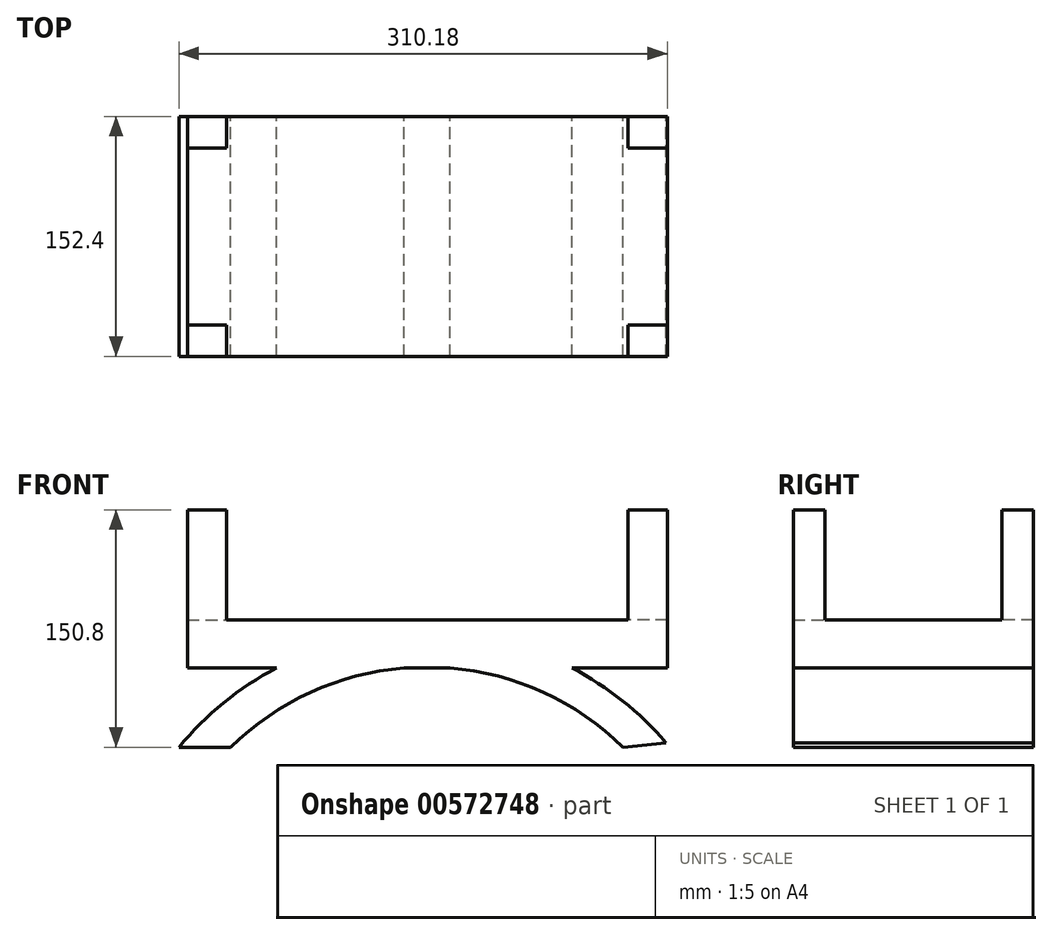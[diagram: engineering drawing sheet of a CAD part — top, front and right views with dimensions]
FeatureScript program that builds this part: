
annotation { "Feature Type Name" : "Feature", "Feature Type Description" : "" }
export const myFeature = defineFeature(function(context is Context, id is Id, definition is map)
    precondition{}
    {
        {
            var Q0;
            Q0=qCreatedBy(makeId("Front.planeOp"),FACE);
            var sketch = newSketch(context, id + "F0", { "sketchPlane" : qUnion([Q0])});
            skLineSegment(sketch, "E0.bottom", {"start": v(152.4, 15.24) * mm, "end": v(-152.4, 15.24) * mm});
            skLineSegment(sketch, "E0.top", {"start": v(152.4, -15.24) * mm, "end": v(-152.4, -15.24) * mm});
            skLineSegment(sketch, "E0.left", {"start": v(152.4, 15.24) * mm, "end": v(152.4, -15.24) * mm});
            skLineSegment(sketch, "E0.right", {"start": v(-152.4, 15.24) * mm, "end": v(-152.4, -15.24) * mm});
            skPoint(sketch, "E0.middle", {"position": v(0, 0) * mm});
            skSolve(sketch);
        }
        {
            var Q0;
            Q0=makeQuery(id+"F0.imprint","IMPRINT",FACE,{"disambiguationData":[TD([[makeQuery(id+"F0.imprint","IMPRINT",EDGE,{"derivedFrom":sQuery(id+"F0.wireOp",EDGE,"E0.bottom")}),1.0]])]});
            extrude(context, id + "F1", {"entities" : qUnion([Q0]), "depth" : 152.4 * mm, "offsetDistance" : 25.4 * mm});
        }
        {
            var Q0;
            Q0=makeQuery(id+"F1.opExtrude","SWEPT_FACE",FACE,{"disambiguationData":[OSD([sQuery(id+"F0.wireOp",EDGE,"E0.bottom")])]});
            var sketch = newSketch(context, id + "F2", { "sketchPlane" : qUnion([Q0])});
            skLineSegment(sketch, "E1.bottom", {"start": v(-152.4, 0) * mm, "end": v(-127.4, 0) * mm});
            skLineSegment(sketch, "E1.top", {"start": v(-152.4, -20) * mm, "end": v(-127.4, -20) * mm});
            skLineSegment(sketch, "E1.left", {"start": v(-152.4, 0) * mm, "end": v(-152.4, -20) * mm});
            skLineSegment(sketch, "E1.right", {"start": v(-127.4, 0) * mm, "end": v(-127.4, -20) * mm});
            skLineSegment(sketch, "E2.bottom", {"start": v(-152.4, -152.4) * mm, "end": v(-127.4, -152.4) * mm});
            skLineSegment(sketch, "E2.top", {"start": v(-152.4, -132.4) * mm, "end": v(-127.4, -132.4) * mm});
            skLineSegment(sketch, "E2.left", {"start": v(-152.4, -152.4) * mm, "end": v(-152.4, -132.4) * mm});
            skLineSegment(sketch, "E2.right", {"start": v(-127.4, -152.4) * mm, "end": v(-127.4, -132.4) * mm});
            skLineSegment(sketch, "E3.bottom", {"start": v(152.4, 0) * mm, "end": v(127.4, 0) * mm});
            skLineSegment(sketch, "E3.top", {"start": v(152.4, -20) * mm, "end": v(127.4, -20) * mm});
            skLineSegment(sketch, "E3.left", {"start": v(152.4, 0) * mm, "end": v(152.4, -20) * mm});
            skLineSegment(sketch, "E3.right", {"start": v(127.4, 0) * mm, "end": v(127.4, -20) * mm});
            skLineSegment(sketch, "E4.bottom", {"start": v(152.4, -152.4) * mm, "end": v(127.4, -152.4) * mm});
            skLineSegment(sketch, "E4.top", {"start": v(152.4, -132.4) * mm, "end": v(127.4, -132.4) * mm});
            skLineSegment(sketch, "E4.left", {"start": v(152.4, -152.4) * mm, "end": v(152.4, -132.4) * mm});
            skLineSegment(sketch, "E4.right", {"start": v(127.4, -152.4) * mm, "end": v(127.4, -132.4) * mm});
            skSolve(sketch);
        }
        {
            var Q0;
            Q0=qSketchRegion(id+"F2",true);
            extrude(context, id + "F3", {"entities" : qUnion([Q0]), "operationType" : NewBodyOperationType.ADD, "depth" : 70 * mm, "offsetDistance" : 25 * mm});
        }
        {
            var Q0;
            Q0=qCreatedBy(makeId("Front.planeOp"),FACE);
            var sketch = newSketch(context, id + "F4", { "sketchPlane" : qUnion([Q0])});
            skArc(sketch, "E5", {"start": v(151.54, -62.73) * mm, "mid": v(-3.78, 7.87) * mm, "end": v(-157.78, -65.56) * mm});
            skLineSegment(sketch, "E6", {"start": v(-157.78, -65.56) * mm, "end": v(-124.87, -65.56) * mm});
            skLineSegment(sketch, "E7", {"start": v(124.23, -65.56) * mm, "end": v(151.54, -62.73) * mm});
            skArc(sketch, "E8", {"start": v(124.23, -65.56) * mm, "mid": v(-0.32, -14.65) * mm, "end": v(-124.87, -65.56) * mm});
            skSolve(sketch);
        }
        {
            var Q0;
            Q0=makeQuery(id+"F4.imprint","IMPRINT",FACE,{"disambiguationData":[TD([[makeQuery(id+"F4.imprint","IMPRINT",EDGE,{"derivedFrom":sQuery(id+"F4.wireOp",EDGE,"E5")}),1.0]])]});
            extrude(context, id + "F5", {"entities" : qUnion([Q0]), "operationType" : NewBodyOperationType.ADD, "depth" : 152.4 * mm, "offsetDistance" : 25.4 * mm});
        }
        {
            var Q0;
            Q0=qCreatedBy(makeId("Front.planeOp"),FACE);
            var sketch = newSketch(context, id + "F6", { "sketchPlane" : qUnion([Q0])});
            skLineSegment(sketch, "E9", {"start": v(-148.6, -3.82) * mm, "end": v(-148.6, -55.17) * mm});
            skSolve(sketch);
        }
        {
            var Q0;
            Q0=qSketchRegion(id+"F6",true);
            var Q1;
            Q1=sQuery(id+"F6.wireOp",EDGE,"E9");
            extrude(context, id + "F7", {"entities" : qUnion([Q0]), "bodyType" : ToolBodyType.SURFACE, "operationType" : NewBodyOperationType.ADD, "surfaceEntities" : qUnion([Q1]), "depth" : 152.4 * mm, "offsetDistance" : 25.4 * mm});
        }
        {
            var Q0;
            Q0=qCreatedBy(makeId("Front.planeOp"),FACE);
            var sketch = newSketch(context, id + "F8", { "sketchPlane" : qUnion([Q0])});
            skLineSegment(sketch, "E10", {"start": v(145.65, -3.53) * mm, "end": v(145.65, -55.63) * mm});
            skSolve(sketch);
        }
        {
            var Q0;
            Q0=qSketchRegion(id+"F8",true);
            var Q1;
            Q1=sQuery(id+"F8.wireOp",EDGE,"E10");
            extrude(context, id + "F9", {"entities" : qUnion([Q0]), "bodyType" : ToolBodyType.SURFACE, "surfaceEntities" : qUnion([Q1]), "depth" : 152.4 * mm, "offsetDistance" : 25.4 * mm});
        }
        {
            var Q0;
            Q0=qCreatedBy(makeId("Front.planeOp"),FACE);
            var sketch = newSketch(context, id + "F10", { "sketchPlane" : qUnion([Q0])});
            skLineSegment(sketch, "E11", {"start": v(-131.92, -4.41) * mm, "end": v(-131.92, -40.95) * mm});
            skLineSegment(sketch, "E12", {"start": v(-119.23, -4.41) * mm, "end": v(-119.23, -30.55) * mm});
            skLineSegment(sketch, "E13", {"start": v(130.2, -3.86) * mm, "end": v(130.2, -42.03) * mm});
            skLineSegment(sketch, "E14", {"start": v(115.77, -3.96) * mm, "end": v(115.77, -30.26) * mm});
            skLineSegment(sketch, "E15", {"start": v(103.09, -3.72) * mm, "end": v(103.09, -21.49) * mm});
            skSolve(sketch);
        }
        {
            var Q0;
            Q0=sQuery(id+"F10.wireOp",EDGE,"E11");
            var Q1;
            Q1=sQuery(id+"F10.wireOp",EDGE,"E12");
            var Q2;
            Q2=sQuery(id+"F10.wireOp",EDGE,"fmFvBnj1-9WQL-bfwK-aXSt-3DoKom3cdEuT");
            var Q3;
            Q3=sQuery(id+"F10.wireOp",EDGE,"LTrpaOaB-8dMR-r95e-0FNB-BjiynQbojh0S");
            var Q4;
            Q4=sQuery(id+"F10.wireOp",EDGE,"17e0a68b-e625-4447-87db-85543a39e309");
            var Q5;
            Q5=sQuery(id+"F10.wireOp",EDGE,"E15");
            var Q6;
            Q6=sQuery(id+"F10.wireOp",EDGE,"E14");
            var Q7;
            Q7=sQuery(id+"F10.wireOp",EDGE,"E13");
            extrude(context, id + "F11", {"bodyType" : ToolBodyType.SURFACE, "surfaceEntities" : qUnion([Q0, Q1, Q2, Q3, Q4, Q5, Q6, Q7]), "depth" : 152.4 * mm, "offsetDistance" : 25.4 * mm});
        }
        {
            var Q0;
            Q0=makeQuery(id+"F1.opExtrude","SWEPT_FACE",FACE,{"disambiguationData":[OSD([sQuery(id+"F0.wireOp",EDGE,"E0.bottom")])]});
            var sketch = newSketch(context, id + "F12", { "sketchPlane" : qUnion([Q0])});
            skLineSegment(sketch, "E16", {"start": v(-152.4, -76.2) * mm, "end": v(152.4, -76.2) * mm});
            skSolve(sketch);
        }
        {
            var Q0;
            Q0=qSketchRegion(id+"F12",true);
            var Q1;
            Q1=sQuery(id+"F12.wireOp",EDGE,"E16");
            extrude(context, id + "F13", {"entities" : qUnion([Q0]), "bodyType" : ToolBodyType.SURFACE, "surfaceEntities" : qUnion([Q1]), "depth" : 1.84 * mm});
        }
    });
